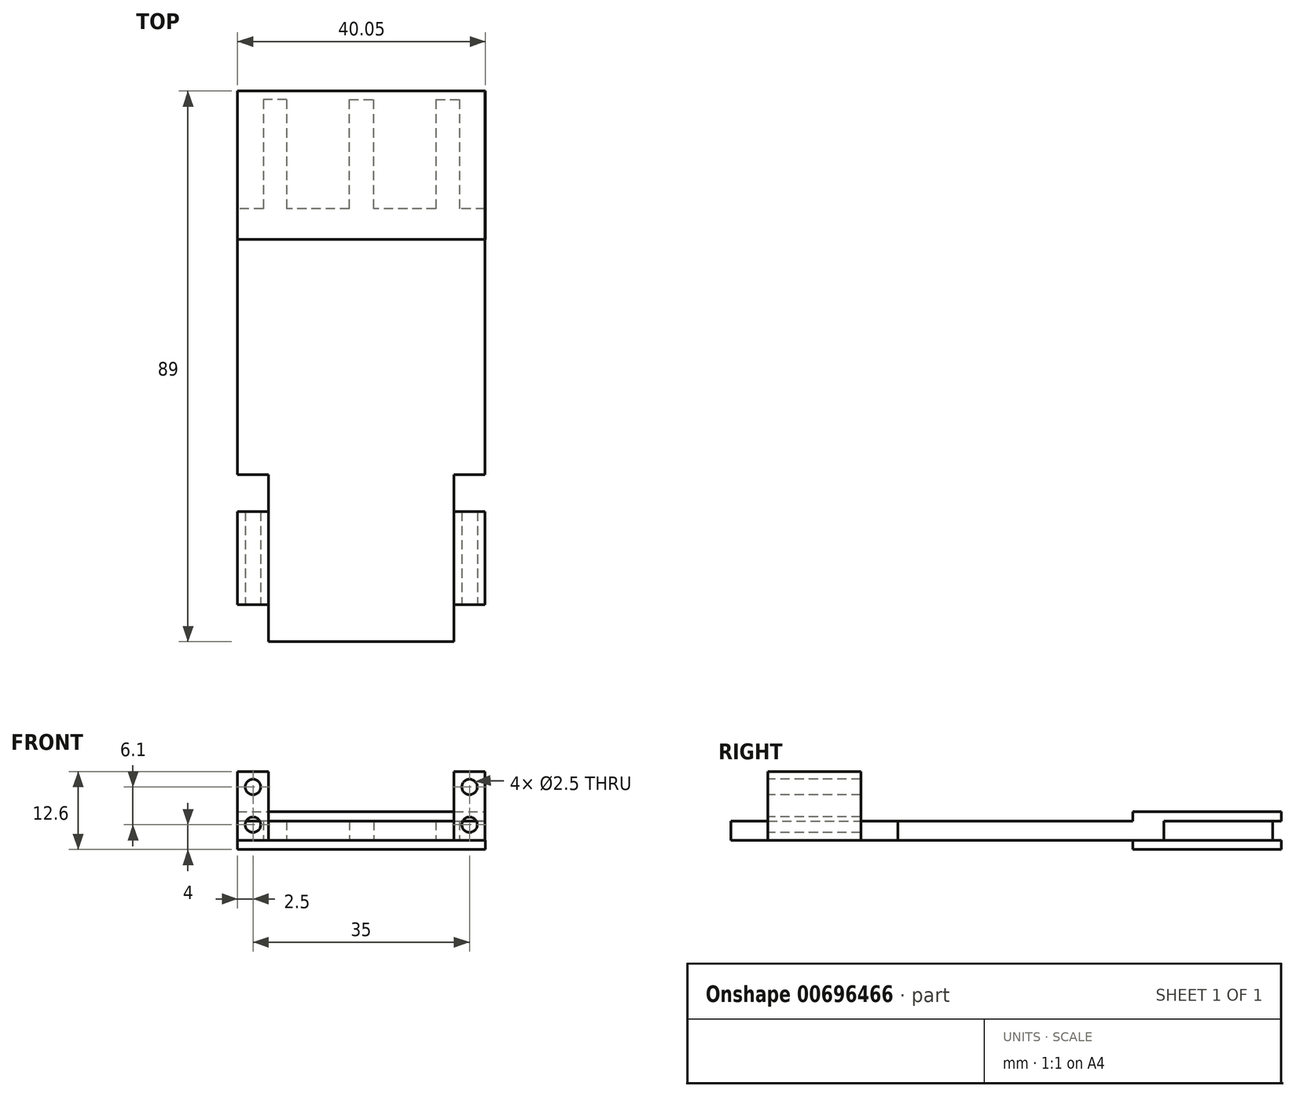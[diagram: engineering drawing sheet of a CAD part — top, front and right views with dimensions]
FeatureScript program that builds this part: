
annotation { "Feature Type Name" : "Feature", "Feature Type Description" : "" }
export const myFeature = defineFeature(function(context is Context, id is Id, definition is map)
    precondition{}
    {
        {
            var Q0;
            Q0=qCreatedBy(makeId("Top.planeOp"),FACE);
            var sketch = newSketch(context, id + "F0", { "sketchPlane" : qUnion([Q0])});
            skLineSegment(sketch, "E0.bottom", {"start": v(20, 35) * mm, "end": v(-20, 35) * mm});
            skLineSegment(sketch, "E0.top", {"start": v(20, -35) * mm, "end": v(-20, -35) * mm});
            skLineSegment(sketch, "E0.left", {"start": v(20, 35) * mm, "end": v(20, -35) * mm});
            skLineSegment(sketch, "E0.right", {"start": v(-20, 35) * mm, "end": v(-20, -35) * mm});
            skPoint(sketch, "E0.middle", {"position": v(0, 0) * mm});
            skLineSegment(sketch, "E1.bottom", {"start": v(-1.95, 35) * mm, "end": v(2, 35) * mm});
            skLineSegment(sketch, "E1.top", {"start": v(-1.95, 52.6) * mm, "end": v(2, 52.6) * mm});
            skLineSegment(sketch, "E1.left", {"start": v(-1.95, 35) * mm, "end": v(-1.95, 52.6) * mm});
            skLineSegment(sketch, "E1.right", {"start": v(2, 35) * mm, "end": v(2, 52.6) * mm});
            skLineSegment(sketch, "E2.bottom", {"start": v(-12.05, 52.6) * mm, "end": v(-15.85, 52.6) * mm});
            skLineSegment(sketch, "E2.top", {"start": v(-12.05, 35) * mm, "end": v(-15.85, 35) * mm});
            skLineSegment(sketch, "E2.left", {"start": v(-12.05, 52.6) * mm, "end": v(-12.05, 35) * mm});
            skLineSegment(sketch, "E2.right", {"start": v(-15.85, 52.6) * mm, "end": v(-15.85, 35) * mm});
            skLineSegment(sketch, "E3.MirrorCS", {"start": v(12.05, 52.6) * mm, "end": v(12.05, 35) * mm});
            skLineSegment(sketch, "E4.MirrorCS", {"start": v(12.05, 35) * mm, "end": v(15.85, 35) * mm});
            skLineSegment(sketch, "E5.MirrorCS", {"start": v(15.85, 52.6) * mm, "end": v(15.85, 35) * mm});
            skLineSegment(sketch, "E6.MirrorCS", {"start": v(12.05, 52.6) * mm, "end": v(15.85, 52.6) * mm});
            skSolve(sketch);
        }
        {
            var Q0;
            {var subQ7=sQuery(id+"F0.wireOp",EDGE,"E3.MirrorCS");Q0=qUnion([makeQuery(id+"F0.imprint","IMPRINT",FACE,{"disambiguationData":[TD([[makeQuery(id+"F0.imprint","IMPRINT",EDGE,{"derivedFrom":sQuery(id+"F0.wireOp",EDGE,"E1.top")}),-1.0]])]}),makeQuery(id+"F0.imprint","IMPRINT",FACE,{"disambiguationData":[TD([[makeQuery(id+"F0.imprint","IMPRINT",EDGE,{"derivedFrom":sQuery(id+"F0.wireOp",EDGE,"E2.bottom")}),1.0]])]}),makeQuery(id+"F0.imprint","IMPRINT",FACE,{"disambiguationData":[TD([[makeQuery(id+"F0.imprint","IMPRINT",EDGE,{"derivedFrom":subQ7}),1.0]])]}),makeQuery(id+"F0.imprint","IMPRINT",FACE,{"disambiguationData":[TD([[makeQuery(id+"F0.imprint","IMPRINT",EDGE,{"derivedFrom":sQuery(id+"F0.wireOp",EDGE,"E0.top")}),-1.0]])]})]);}
            extrude(context, id + "F1", {"entities" : qUnion([Q0]), "depth" : 3.1 * mm, "offsetDistance" : 25 * mm});
        }
        {
            var Q0;
            Q0=makeQuery(id+"F1.opExtrude","CAP_FACE",FACE,{"disambiguationData":[OSD([sQuery(id+"F0.wireOp",EDGE,"E0.bottom"),sQuery(id+"F0.wireOp",EDGE,"E0.top"),sQuery(id+"F0.wireOp",EDGE,"E0.left"),sQuery(id+"F0.wireOp",EDGE,"E0.right"),sQuery(id+"F0.wireOp",EDGE,"E1.top"),sQuery(id+"F0.wireOp",EDGE,"E1.left"),sQuery(id+"F0.wireOp",EDGE,"E1.right"),sQuery(id+"F0.wireOp",EDGE,"E2.bottom"),sQuery(id+"F0.wireOp",EDGE,"E2.left"),sQuery(id+"F0.wireOp",EDGE,"E2.right"),sQuery(id+"F0.wireOp",EDGE,"E3.MirrorCS"),sQuery(id+"F0.wireOp",EDGE,"E5.MirrorCS"),sQuery(id+"F0.wireOp",EDGE,"E6.MirrorCS")])],"isStart":false});
            var sketch = newSketch(context, id + "F2", { "sketchPlane" : qUnion([Q0])});
            skLineSegment(sketch, "E7.bottom", {"start": v(-20, 30) * mm, "end": v(20, 30) * mm});
            skLineSegment(sketch, "E7.top", {"start": v(-20, 54) * mm, "end": v(20, 54) * mm});
            skLineSegment(sketch, "E7.left", {"start": v(-20, 30) * mm, "end": v(-20, 54) * mm});
            skLineSegment(sketch, "E7.right", {"start": v(20, 30) * mm, "end": v(20, 54) * mm});
            skSolve(sketch);
        }
        {
            var Q0;
            Q0 = qSketchRegion(id + "F2", true);
            extrude(context, id + "F3", {"entities" : qUnion([Q0]), "operationType" : NewBodyOperationType.ADD, "depth" : 1.5 * mm, "offsetDistance" : 25 * mm});
        }
        {
            var Q0;
            Q0=makeQuery(id+"F1.opExtrude","CAP_FACE",FACE,{"disambiguationData":[OSD([sQuery(id+"F0.wireOp",EDGE,"E0.bottom"),sQuery(id+"F0.wireOp",EDGE,"E0.top"),sQuery(id+"F0.wireOp",EDGE,"E0.left"),sQuery(id+"F0.wireOp",EDGE,"E0.right"),sQuery(id+"F0.wireOp",EDGE,"E1.top"),sQuery(id+"F0.wireOp",EDGE,"E1.left"),sQuery(id+"F0.wireOp",EDGE,"E1.right"),sQuery(id+"F0.wireOp",EDGE,"E2.bottom"),sQuery(id+"F0.wireOp",EDGE,"E2.left"),sQuery(id+"F0.wireOp",EDGE,"E2.right"),sQuery(id+"F0.wireOp",EDGE,"E3.MirrorCS"),sQuery(id+"F0.wireOp",EDGE,"E5.MirrorCS"),sQuery(id+"F0.wireOp",EDGE,"E6.MirrorCS")])],"isStart":true});
            var sketch = newSketch(context, id + "F4", { "sketchPlane" : qUnion([Q0])});
            skLineSegment(sketch, "E8.bottom", {"start": v(-20, -30) * mm, "end": v(20.05, -30) * mm});
            skLineSegment(sketch, "E8.top", {"start": v(-20, -54) * mm, "end": v(20.05, -54) * mm});
            skLineSegment(sketch, "E8.left", {"start": v(-20, -30) * mm, "end": v(-20, -54) * mm});
            skLineSegment(sketch, "E8.right", {"start": v(20.05, -30) * mm, "end": v(20.05, -54) * mm});
            skSolve(sketch);
        }
        {
            var Q0;
            {var subQ17=sQuery(id+"F4.wireOp",EDGE,"E8.top");Q0=makeQuery(id+"F4.imprint","IMPRINT",FACE,{"disambiguationData":[TD([[makeQuery(id+"F4.imprint","IMPRINT",EDGE,{"derivedFrom":subQ17}),1.0]])]});}
            var Q1;
            Q1=makeQuery(id+"F4.imprint","IMPRINT",FACE,{"disambiguationData":[TD([[makeQuery(id+"F4.imprint","IMPRINT",EDGE,{"derivedFrom":makeQuery(id+"F1.opExtrude","CAP_EDGE",EDGE,{"disambiguationData":[OSD([sQuery(id+"F0.wireOp",EDGE,"E1.top")])],"isStart":true})}),1.0]])]});
            extrude(context, id + "F5", {"entities" : qUnion([Q0, Q1]), "operationType" : NewBodyOperationType.ADD, "depth" : 1.5 * mm, "offsetDistance" : 25 * mm});
        }
        {
            var Q0;
            Q0=makeQuery(id+"F1.opExtrude","CAP_FACE",FACE,{"disambiguationData":[OSD([sQuery(id+"F0.wireOp",EDGE,"E0.bottom"),sQuery(id+"F0.wireOp",EDGE,"E0.top"),sQuery(id+"F0.wireOp",EDGE,"E0.left"),sQuery(id+"F0.wireOp",EDGE,"E0.right"),sQuery(id+"F0.wireOp",EDGE,"E1.top"),sQuery(id+"F0.wireOp",EDGE,"E1.left"),sQuery(id+"F0.wireOp",EDGE,"E1.right"),sQuery(id+"F0.wireOp",EDGE,"E2.bottom"),sQuery(id+"F0.wireOp",EDGE,"E2.left"),sQuery(id+"F0.wireOp",EDGE,"E2.right"),sQuery(id+"F0.wireOp",EDGE,"E3.MirrorCS"),sQuery(id+"F0.wireOp",EDGE,"E5.MirrorCS"),sQuery(id+"F0.wireOp",EDGE,"E6.MirrorCS")])],"isStart":false});
            var sketch = newSketch(context, id + "F6", { "sketchPlane" : qUnion([Q0])});
            skLineSegment(sketch, "E9.bottom", {"start": v(20, -29) * mm, "end": v(15, -29) * mm});
            skLineSegment(sketch, "E9.top", {"start": v(20, -14) * mm, "end": v(15, -14) * mm});
            skLineSegment(sketch, "E9.left", {"start": v(20, -29) * mm, "end": v(20, -14) * mm});
            skLineSegment(sketch, "E9.right", {"start": v(15, -29) * mm, "end": v(15, -14) * mm});
            skLineSegment(sketch, "E10", {"start": v(0, 30) * mm, "end": v(0, -35) * mm, "construction": true});
            skLineSegment(sketch, "E11.MirrorCS", {"start": v(-15, -29) * mm, "end": v(-15, -14) * mm});
            skLineSegment(sketch, "E12.MirrorCS", {"start": v(-20, -14) * mm, "end": v(-15, -14) * mm});
            skLineSegment(sketch, "E13.MirrorCS", {"start": v(-20, -29) * mm, "end": v(-20, -14) * mm});
            skLineSegment(sketch, "E14.MirrorCS", {"start": v(-20, -29) * mm, "end": v(-15, -29) * mm});
            skSolve(sketch);
        }
        {
            var Q0;
            Q0 = qSketchRegion(id + "F6", true);
            extrude(context, id + "F7", {"entities" : qUnion([Q0]), "operationType" : NewBodyOperationType.ADD, "depth" : 8 * mm, "offsetDistance" : 25 * mm});
        }
        {
            var Q0;
            Q0=makeQuery(id+"F1.opExtrude","CAP_FACE",FACE,{"disambiguationData":[OSD([sQuery(id+"F0.wireOp",EDGE,"E0.bottom"),sQuery(id+"F0.wireOp",EDGE,"E0.top"),sQuery(id+"F0.wireOp",EDGE,"E0.left"),sQuery(id+"F0.wireOp",EDGE,"E0.right"),sQuery(id+"F0.wireOp",EDGE,"E1.top"),sQuery(id+"F0.wireOp",EDGE,"E1.left"),sQuery(id+"F0.wireOp",EDGE,"E1.right"),sQuery(id+"F0.wireOp",EDGE,"E2.bottom"),sQuery(id+"F0.wireOp",EDGE,"E2.left"),sQuery(id+"F0.wireOp",EDGE,"E2.right"),sQuery(id+"F0.wireOp",EDGE,"E3.MirrorCS"),sQuery(id+"F0.wireOp",EDGE,"E5.MirrorCS"),sQuery(id+"F0.wireOp",EDGE,"E6.MirrorCS")])],"isStart":false});
            var sketch = newSketch(context, id + "F8", { "sketchPlane" : qUnion([Q0])});
            skLineSegment(sketch, "E15.bottom", {"start": v(15, -29) * mm, "end": v(20, -29) * mm});
            skLineSegment(sketch, "E15.top", {"start": v(15, -35) * mm, "end": v(20, -35) * mm});
            skLineSegment(sketch, "E15.left", {"start": v(15, -29) * mm, "end": v(15, -35) * mm});
            skLineSegment(sketch, "E15.right", {"start": v(20, -29) * mm, "end": v(20, -35) * mm});
            skLineSegment(sketch, "E16.bottom", {"start": v(15, -14) * mm, "end": v(20, -14) * mm});
            skLineSegment(sketch, "E16.top", {"start": v(15, -8) * mm, "end": v(20, -8) * mm});
            skLineSegment(sketch, "E16.left", {"start": v(15, -14) * mm, "end": v(15, -8) * mm});
            skLineSegment(sketch, "E16.right", {"start": v(20, -14) * mm, "end": v(20, -8) * mm});
            skLineSegment(sketch, "E17", {"start": v(0, 30) * mm, "end": v(0, -35) * mm, "construction": true});
            skLineSegment(sketch, "E18.MirrorCS", {"start": v(-20, -14) * mm, "end": v(-20, -8) * mm});
            skLineSegment(sketch, "E19.MirrorCS", {"start": v(-15, -8) * mm, "end": v(-20, -8) * mm});
            skLineSegment(sketch, "E20.MirrorCS", {"start": v(-15, -14) * mm, "end": v(-15, -8) * mm});
            skLineSegment(sketch, "E21.MirrorCS", {"start": v(-15, -14) * mm, "end": v(-20, -14) * mm});
            skLineSegment(sketch, "E22.MirrorCS", {"start": v(-15, -29) * mm, "end": v(-20, -29) * mm});
            skLineSegment(sketch, "E23.MirrorCS", {"start": v(-15, -29) * mm, "end": v(-15, -35) * mm});
            skLineSegment(sketch, "E24.MirrorCS", {"start": v(-15, -35) * mm, "end": v(-20, -35) * mm});
            skLineSegment(sketch, "E25.MirrorCS", {"start": v(-20, -29) * mm, "end": v(-20, -35) * mm});
            skSolve(sketch);
        }
        {
            var Q0;
            Q0 = qSketchRegion(id + "F8", true);
            extrude(context, id + "F9", {"entities" : qUnion([Q0]), "operationType" : NewBodyOperationType.REMOVE, "endBound" : BoundingType.THROUGH_ALL, "oppositeDirection" : true, "depth" : 25 * mm, "offsetDistance" : 25 * mm});
        }
        {
            var Q0;
            Q0=makeQuery(id+"F9.boolean.opBoolean","MERGE",FACE,{"derivedFrom":[makeQuery(id+"F7.opExtrude","SWEPT_FACE",FACE,{"disambiguationData":[OSD([sQuery(id+"F6.wireOp",EDGE,"E9.bottom")])]}),makeQuery(id+"F9.opExtrude","SWEPT_FACE",FACE,{"disambiguationData":[OSD([sQuery(id+"F8.wireOp",EDGE,"E15.bottom")])]})]});
            var sketch = newSketch(context, id + "F10", { "sketchPlane" : qUnion([Q0])});
            skLineSegment(sketch, "E26", {"start": v(17.5, 11.1) * mm, "end": v(17.5, 0) * mm, "construction": true});
            skCircle(sketch, "E27", {"center": v(17.5, 8.6) * mm, "radius": 1.25 * mm});
            skCircle(sketch, "E28", {"center": v(17.5, 2.5) * mm, "radius": 1.25 * mm});
            skSolve(sketch);
        }
        {
            var Q0;
            Q0 = qSketchRegion(id + "F10", true);
            extrude(context, id + "F11", {"entities" : qUnion([Q0]), "operationType" : NewBodyOperationType.REMOVE, "endBound" : BoundingType.UP_TO_NEXT, "oppositeDirection" : true, "depth" : 25 * mm, "offsetDistance" : 25 * mm});
        }
        {
            var Q0;
            Q0=makeQuery(id+"F9.boolean.opBoolean","MERGE",FACE,{"derivedFrom":[makeQuery(id+"F7.opExtrude","SWEPT_FACE",FACE,{"disambiguationData":[OSD([sQuery(id+"F6.wireOp",EDGE,"E14.MirrorCS")])]}),makeQuery(id+"F9.opExtrude","SWEPT_FACE",FACE,{"disambiguationData":[OSD([sQuery(id+"F8.wireOp",EDGE,"E22.MirrorCS")])]})]});
            var sketch = newSketch(context, id + "F12", { "sketchPlane" : qUnion([Q0])});
            skLineSegment(sketch, "E29", {"start": v(-17.5, 11.1) * mm, "end": v(-17.5, 0) * mm, "construction": true});
            skCircle(sketch, "E30", {"center": v(-17.5, 8.6) * mm, "radius": 1.25 * mm});
            skCircle(sketch, "E31", {"center": v(-17.5, 2.5) * mm, "radius": 1.25 * mm});
            skSolve(sketch);
        }
        {
            var Q0;
            Q0 = qSketchRegion(id + "F12", true);
            extrude(context, id + "F13", {"entities" : qUnion([Q0]), "operationType" : NewBodyOperationType.REMOVE, "endBound" : BoundingType.UP_TO_NEXT, "oppositeDirection" : true, "depth" : 25 * mm, "offsetDistance" : 25 * mm});
        }
    });
